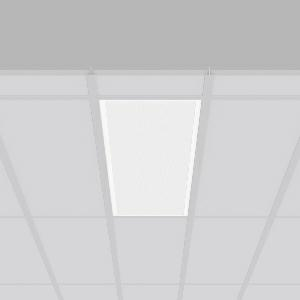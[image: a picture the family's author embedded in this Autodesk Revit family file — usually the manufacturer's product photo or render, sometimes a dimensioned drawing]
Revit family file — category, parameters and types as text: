
# Revit family: sidelite_eco_672369_002_4c0c
name_source: partatom
category: Lighting Fixtures
units: mm (PartAtom-declared; Revit-internal decimal feet)

## family parameters
Cut with Voids When Loaded = No
Host = Face
Light Source = No
Part Type = Normal
Room Calculation Point = No
Round Connector Dimension = Use Diameter
Shared = No

## types (1)
- SIDELITE ECO (1 x LED Modul 830, 3200 lm, 3000)
    Apparent Load = 29 VA
    CIE Flux Codes = 59 87 97 100 100
    Color Rendering = 80
    Color Temperature = 3000
    Default Elevation = 1800 mm
    Description = Series: SIDELITE ECO
Highly economical recessed luminaire with progressive LED technology. For escape route illumination. Frame made of aluminium, powder-coated. Diffuser plastic microprismatic. Lightguide and diffuser made of non-yellowing plastic (PMMA). Lateral light emission (RZB SIDELITE technology) for homogeneous light distribution. External driver. Self-contained system with automatic self-test. External driver with simple plug-in locking system. Extended connection cable (1.90 m). 
Colour: white
Length: 1195 mm
Width: 295 mm
Cut-out length: 1170 mm
Cut-out width: 270 mm
Recess height: 160 mm
Luminaire: recess height: 40 mm
Weight: 4.4 kg
Operating mode: maintained power mode
Duration time: 8 h
Lamp: LED
Socket: without socket
Colour temperature: 3000K
Colour rendering index (CRI): 80
System power: 29 W
Rated luminous flux: 3200 lm
Luminous flux, emergency: 220 lm
System power, emergency: -
Control gear: Regulated power supply
Protection class: I
Type of protection: IP 40
    Height = 0 mm  [stored 0 ft]
    Lamp = 1 x LED Modul 830
    Lamp Light Flux = 3200 lm
    Lamp count = 1
    Length = 1195 mm
    Lifetime = 50000 h
    Luminous efficacy = 110 lm/W
    Manufacturer = RZB
    ModVariant = No
    Model = 672369.002
    Mounting Place = Ceiling
    Mounting Type = Recessed
    Number of Poles = 1
    OnlyDefault = Yes
    Power Factor = 1
    Product Name = SIDELITE ECO
    Product group = Recessed modular luminaires
    ProductGroupID = 406
    Protection Class = Protection class I
    Protection Degree = IP 40
    RLX_Detail_Level = 1
    RLX_Emergency_Light_Flux = 220 lm
    RLX_Emergency_Type = 3
    RLX_Emergency_Type_DB = Yes
    RlxData = <blob elided: 34633 chars, md5=44d6b1bd>
    Socket = socket
    Standby Power = 0 W
    System Light Flux = 3200 lm
    System Power = 29 W
    Type Comments = Product without accessories
    Type Image = 312366.002.jpg
    URL = http://relux.com
    VarID = ---
    Voltage = 230 V
    Voltage Range = 220-240 V
    Weight = 0.00 kg
    Width = 295 mm

note: [stored X ft] marks values corroborated as IEEE doubles in the binary element streams (Revit-internal decimal feet)

## geometry (parser evidence)
native form markers: Blend x4, Sweep x11
no freeform markers — native parametric forms only
